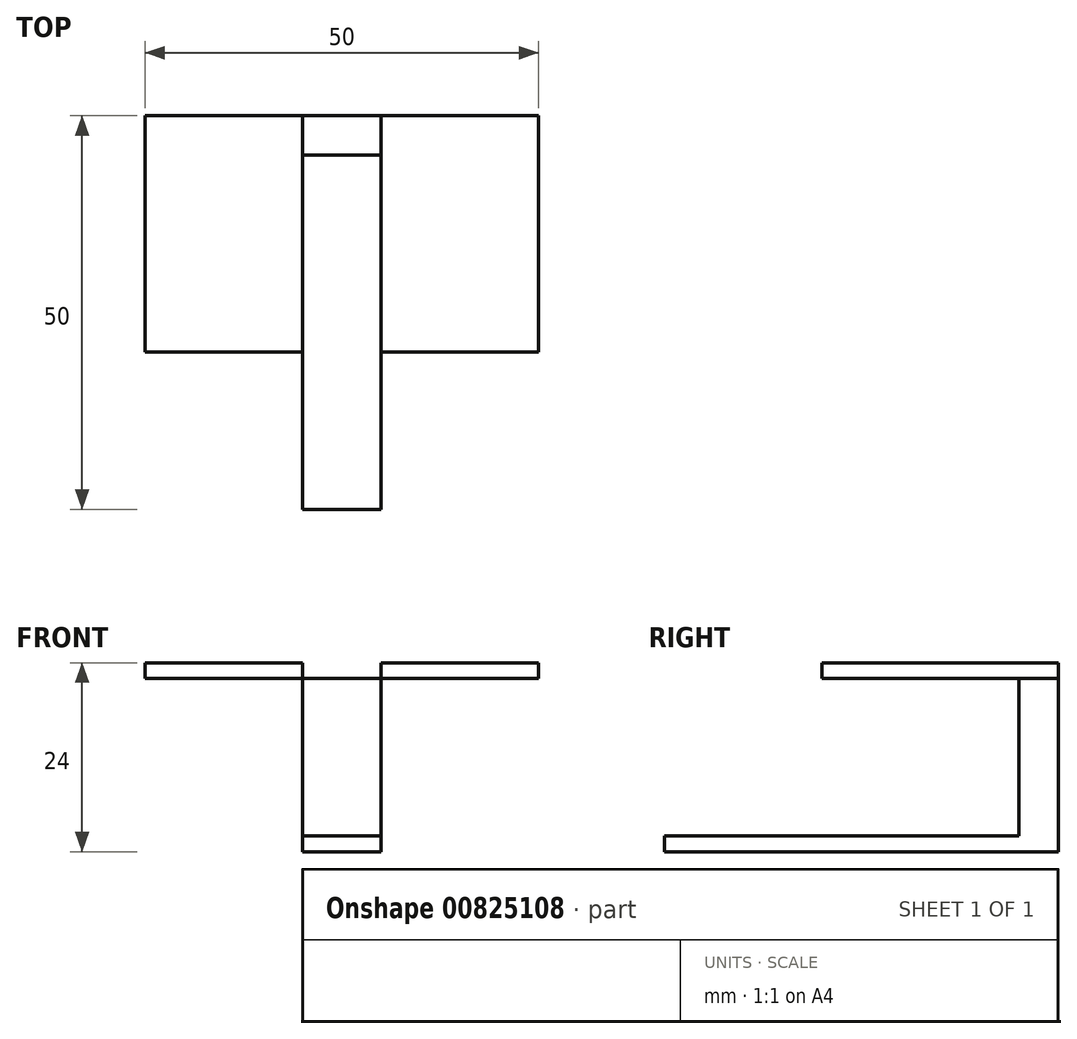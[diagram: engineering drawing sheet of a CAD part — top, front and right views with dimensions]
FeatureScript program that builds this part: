
annotation { "Feature Type Name" : "Feature", "Feature Type Description" : "" }
export const myFeature = defineFeature(function(context is Context, id is Id, definition is map)
    precondition{}
    {
        {
            var Q0;
            Q0=qCreatedBy(makeId("Top.planeOp"),FACE);
            var sketch = newSketch(context, id + "F0", { "sketchPlane" : qUnion([Q0])});
            skLineSegment(sketch, "E0.bottom", {"start": v(5, -15) * mm, "end": v(-5, -15) * mm});
            skLineSegment(sketch, "E0.top", {"start": v(5, 15) * mm, "end": v(-5, 15) * mm});
            skLineSegment(sketch, "E0.left", {"start": v(5, -35) * mm, "end": v(5, 15) * mm});
            skLineSegment(sketch, "E0.right", {"start": v(-5, -35) * mm, "end": v(-5, 15) * mm});
            skPoint(sketch, "E0.middle", {"position": v(0, 0) * mm});
            skLineSegment(sketch, "E1.bottom", {"start": v(-5, 15) * mm, "end": v(5, 15) * mm});
            skLineSegment(sketch, "E1.top", {"start": v(-5, 10) * mm, "end": v(5, 10) * mm});
            skLineSegment(sketch, "E1.left", {"start": v(-5, 15) * mm, "end": v(-5, 10) * mm});
            skLineSegment(sketch, "E1.right", {"start": v(5, 15) * mm, "end": v(5, 10) * mm});
            skLineSegment(sketch, "E2.bottom", {"start": v(25, 15) * mm, "end": v(-25, 15) * mm});
            skLineSegment(sketch, "E2.top", {"start": v(25, -15) * mm, "end": v(-25, -15) * mm});
            skLineSegment(sketch, "E2.left", {"start": v(25, 15) * mm, "end": v(25, -15) * mm});
            skLineSegment(sketch, "E2.right", {"start": v(-25, 15) * mm, "end": v(-25, -15) * mm});
            skLineSegment(sketch, "E3", {"start": v(-5, -35) * mm, "end": v(5, -35) * mm});
            skSolve(sketch);
        }
        {
            var Q0;
            {var subQ4=sQuery(id+"F0.wireOp",EDGE,"E3");Q0=makeQuery(id+"F0.imprint","IMPRINT",FACE,{"disambiguationData":[TD([[makeQuery(id+"F0.imprint","IMPRINT",EDGE,{"derivedFrom":subQ4}),1.0]])]});}
            var Q1;
            {var subQ0=sQuery(id+"F0.wireOp",EDGE,"E1.top");Q1=makeQuery(id+"F0.imprint","IMPRINT",FACE,{"disambiguationData":[TD([[makeQuery(id+"F0.imprint","IMPRINT",EDGE,{"derivedFrom":subQ0}),-1.0]])]});}
            var Q2;
            Q2=makeQuery(id+"F0.imprint","IMPRINT",FACE,{"disambiguationData":[TD([[makeQuery(id+"F0.imprint","IMPRINT",EDGE,{"derivedFrom":sQuery(id+"F0.wireOp",EDGE,"E1.top")}),1.0]])]});
            extrude(context, id + "F1", {"entities" : qUnion([Q0, Q1, Q2]), "depth" : 2 * mm, "offsetDistance" : 25 * mm});
        }
        {
            var Q0;
            Q0=makeQuery(id+"F1.opExtrude","CAP_FACE",FACE,{"disambiguationData":[OSD([sQuery(id+"F0.wireOp",EDGE,"E0.left"),sQuery(id+"F0.wireOp",EDGE,"E0.right"),sQuery(id+"F0.wireOp",EDGE,"E1.left"),sQuery(id+"F0.wireOp",EDGE,"E1.right"),sQuery(id+"F0.wireOp",EDGE,"E2.bottom"),sQuery(id+"F0.wireOp",EDGE,"E3")])],"isStart":false});
            var sketch = newSketch(context, id + "F2", { "sketchPlane" : qUnion([Q0])});
            skLineSegment(sketch, "E4.0.0", {"start": v(5, 10) * mm, "end": v(5, 15) * mm});
            skLineSegment(sketch, "E4.0.1", {"start": v(5, 15) * mm, "end": v(-5, 15) * mm});
            skLineSegment(sketch, "E4.0.2", {"start": v(-5, 15) * mm, "end": v(-5, 10) * mm});
            skLineSegment(sketch, "E4.0.3", {"start": v(-5, 10) * mm, "end": v(5, 10) * mm});
            skSolve(sketch);
        }
        {
            var Q0;
            Q0=makeQuery(id+"F2.imprint","IMPRINT",FACE,{"disambiguationData":[TD([[makeQuery(id+"F2.imprint","IMPRINT",EDGE,{"derivedFrom":sQuery(id+"F2.wireOp",EDGE,"E4.0.0")}),1.0]])]});
            extrude(context, id + "F3", {"entities" : qUnion([Q0]), "operationType" : NewBodyOperationType.ADD, "depth" : 20 * mm, "offsetDistance" : 25 * mm});
        }
        {
            var Q0;
            Q0=makeQuery(id+"F3.opExtrude","CAP_FACE",FACE,{"disambiguationData":[OSD([sQuery(id+"F2.wireOp",EDGE,"E4.0.0"),sQuery(id+"F2.wireOp",EDGE,"E4.0.1"),sQuery(id+"F2.wireOp",EDGE,"E4.0.2"),sQuery(id+"F2.wireOp",EDGE,"E4.0.3")])],"isStart":false});
            var sketch = newSketch(context, id + "F4", { "sketchPlane" : qUnion([Q0])});
            skLineSegment(sketch, "E5.0.0", {"start": v(25, 15) * mm, "end": v(5, 15) * mm});
            skLineSegment(sketch, "E5.0.1", {"start": v(5, 15) * mm, "end": v(5, 10) * mm});
            skLineSegment(sketch, "E5.0.2", {"start": v(5, 10) * mm, "end": v(5, -15) * mm});
            skLineSegment(sketch, "E5.0.3", {"start": v(5, -15) * mm, "end": v(25, -15) * mm});
            skLineSegment(sketch, "E5.0.4", {"start": v(25, -15) * mm, "end": v(25, 15) * mm});
            skLineSegment(sketch, "E5.1.0", {"start": v(-25, -15) * mm, "end": v(-5, -15) * mm});
            skLineSegment(sketch, "E5.1.1", {"start": v(-5, -15) * mm, "end": v(-5, 10) * mm});
            skLineSegment(sketch, "E5.1.2", {"start": v(-5, 10) * mm, "end": v(-5, 15) * mm});
            skLineSegment(sketch, "E5.1.3", {"start": v(-5, 15) * mm, "end": v(-25, 15) * mm});
            skLineSegment(sketch, "E5.1.4", {"start": v(-25, 15) * mm, "end": v(-25, -15) * mm});
            skLineSegment(sketch, "E5.2.0", {"start": v(5, 10) * mm, "end": v(5, 15) * mm});
            skLineSegment(sketch, "E5.2.1", {"start": v(5, 15) * mm, "end": v(-5, 15) * mm});
            skLineSegment(sketch, "E5.2.2", {"start": v(-5, 15) * mm, "end": v(-5, 10) * mm});
            skLineSegment(sketch, "E5.2.3", {"start": v(-5, 10) * mm, "end": v(5, 10) * mm});
            skLineSegment(sketch, "E5.3.0", {"start": v(-5, 10) * mm, "end": v(-5, -15) * mm});
            skLineSegment(sketch, "E5.3.1", {"start": v(-5, -15) * mm, "end": v(-5, -15) * mm});
            skLineSegment(sketch, "E5.3.2", {"start": v(-5, -15) * mm, "end": v(5, -15) * mm});
            skLineSegment(sketch, "E5.3.3", {"start": v(5, -15) * mm, "end": v(5, 10) * mm});
            skLineSegment(sketch, "E5.3.4", {"start": v(5, 10) * mm, "end": v(-5, 10) * mm});
            skSolve(sketch);
        }
        {
            var Q0;
            Q0=makeQuery(id+"F4.imprint","IMPRINT",FACE,{"disambiguationData":[TD([[makeQuery(id+"F4.imprint","IMPRINT",EDGE,{"derivedFrom":sQuery(id+"F4.wireOp",EDGE,"E5.1.0")}),1.0]])]});
            var Q1;
            Q1=makeQuery(id+"F4.imprint","IMPRINT",FACE,{"disambiguationData":[TD([[makeQuery(id+"F4.imprint","IMPRINT",EDGE,{"derivedFrom":sQuery(id+"F4.wireOp",EDGE,"E5.3.0")}),1.0]])]});
            var Q2;
            Q2=makeQuery(id+"F4.imprint","IMPRINT",FACE,{"disambiguationData":[TD([[makeQuery(id+"F4.imprint","IMPRINT",EDGE,{"derivedFrom":sQuery(id+"F4.wireOp",EDGE,"E5.2.0")}),1.0]])]});
            var Q3;
            Q3=makeQuery(id+"F4.imprint","IMPRINT",FACE,{"disambiguationData":[TD([[makeQuery(id+"F4.imprint","IMPRINT",EDGE,{"derivedFrom":sQuery(id+"F4.wireOp",EDGE,"E5.0.0")}),1.0]])]});
            extrude(context, id + "F5", {"entities" : qUnion([Q0, Q1, Q2, Q3]), "operationType" : NewBodyOperationType.ADD, "depth" : 2 * mm, "offsetDistance" : 25 * mm});
        }
    });
